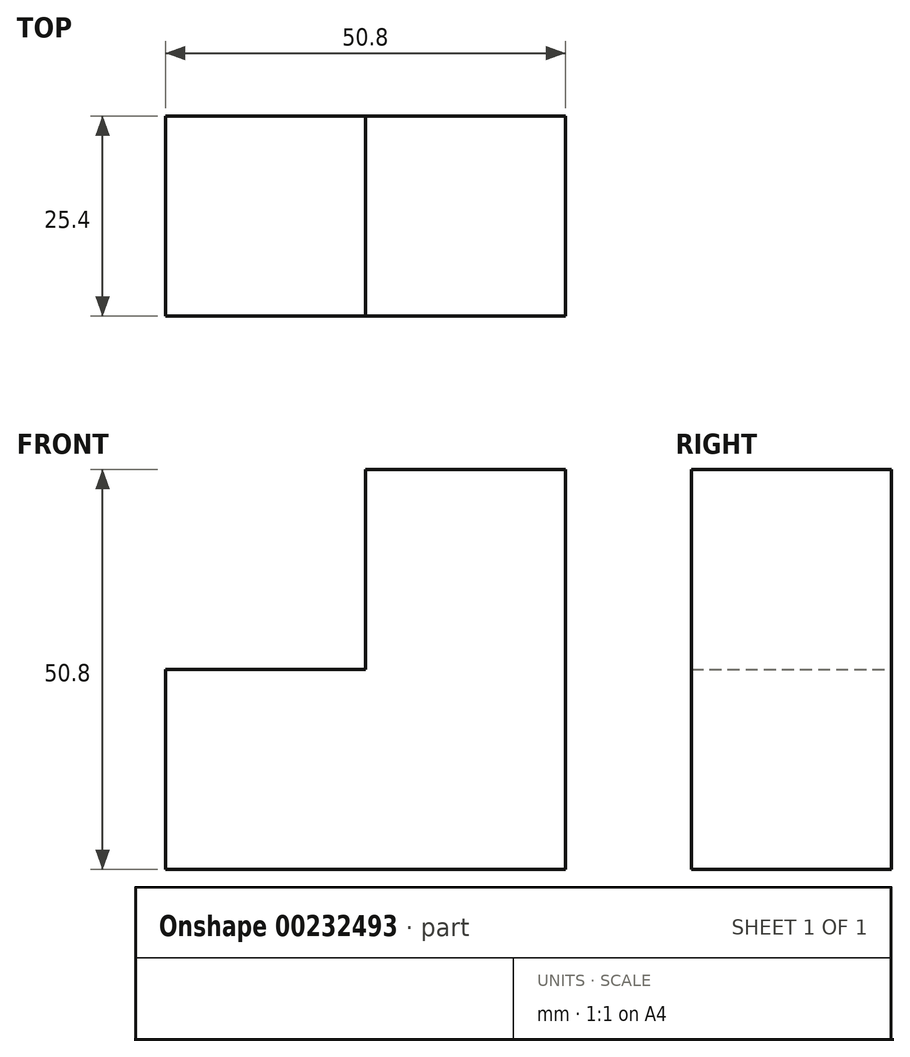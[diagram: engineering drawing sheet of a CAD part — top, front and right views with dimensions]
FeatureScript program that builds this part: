
annotation { "Feature Type Name" : "Feature", "Feature Type Description" : "" }
export const myFeature = defineFeature(function(context is Context, id is Id, definition is map)
    precondition{}
    {
        {
            var Q0;
            Q0=qCreatedBy(makeId("Front.planeOp"),FACE);
            var sketch = newSketch(context, id + "F0", { "sketchPlane" : qUnion([Q0])});
            skLineSegment(sketch, "E0", {"start": v(-50.8, 0) * mm, "end": v(0, 0) * mm});
            skLineSegment(sketch, "E1", {"start": v(0, 0) * mm, "end": v(0, 50.8) * mm});
            skLineSegment(sketch, "E2", {"start": v(0, 50.8) * mm, "end": v(-25.4, 50.8) * mm});
            skLineSegment(sketch, "E3", {"start": v(-25.4, 50.8) * mm, "end": v(-25.4, 25.4) * mm});
            skLineSegment(sketch, "E4", {"start": v(-25.4, 25.4) * mm, "end": v(-50.8, 25.4) * mm});
            skLineSegment(sketch, "E5", {"start": v(-50.8, 25.4) * mm, "end": v(-50.8, 0) * mm});
            skSolve(sketch);
        }
        {
            var Q0;
            Q0=makeQuery(id+"F0.imprint","IMPRINT",FACE,{"disambiguationData":[TD([[makeQuery(id+"F0.imprint","IMPRINT",EDGE,{"derivedFrom":sQuery(id+"F0.wireOp",EDGE,"E0")}),1.0]])]});
            extrude(context, id + "F1", {"entities" : qUnion([Q0]), "depth" : 25.4 * mm});
        }
    });
